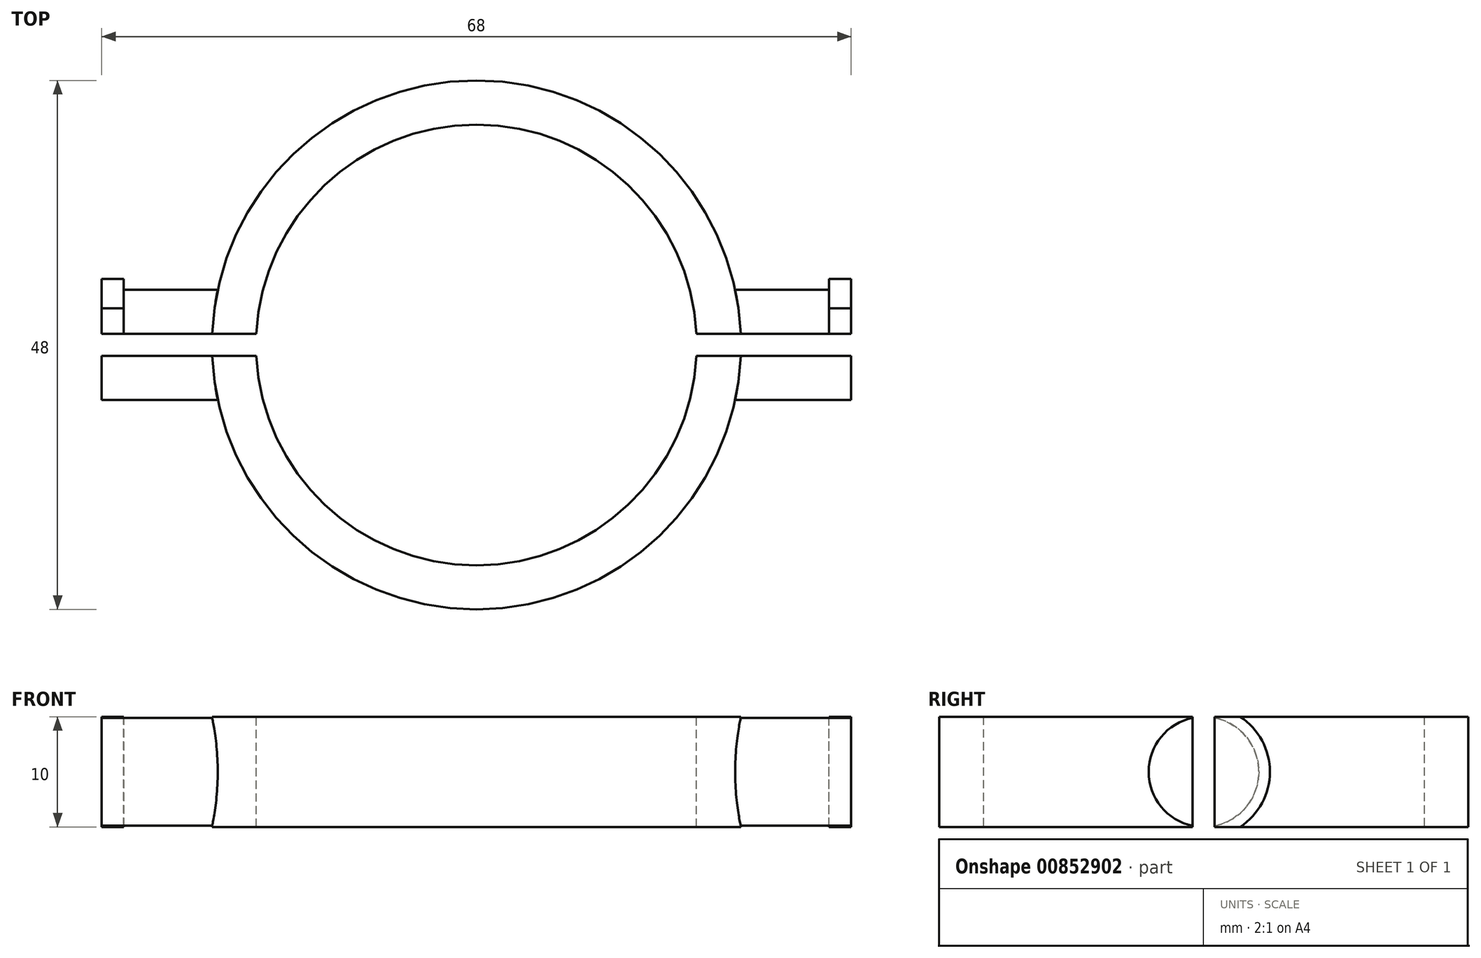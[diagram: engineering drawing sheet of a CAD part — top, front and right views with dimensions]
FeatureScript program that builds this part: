
annotation { "Feature Type Name" : "Feature", "Feature Type Description" : "" }
export const myFeature = defineFeature(function(context is Context, id is Id, definition is map)
    precondition{}
    {
        {
            assignVariable(context, id + "F0", {"name" : "MountDiameter", "anyValue" : 10});
        }
        {
            var Q0;
            Q0=qCreatedBy(makeId("Top.planeOp"),FACE);
            var sketch = newSketch(context, id + "F1", { "sketchPlane" : qUnion([Q0])});
            skCircle(sketch, "E0", {"center": v(0, 0) * mm, "radius": 20 * mm});
            skCircle(sketch, "E1", {"center": v(0, 0) * mm, "radius": 24 * mm});
            skLineSegment(sketch, "E2.bottom", {"start": v(23.47, 5) * mm, "end": v(34, 5) * mm});
            skLineSegment(sketch, "E2.top", {"start": v(23.47, -5) * mm, "end": v(34, -5) * mm});
            skLineSegment(sketch, "E2.left", {"start": v(23.47, 5) * mm, "end": v(23.47, -5) * mm});
            skLineSegment(sketch, "E2.right", {"start": v(34, 5) * mm, "end": v(34, -5) * mm});
            skLineSegment(sketch, "E3.bottom", {"start": v(-23.47, 5) * mm, "end": v(-34, 5) * mm});
            skLineSegment(sketch, "E3.top", {"start": v(-23.47, -5) * mm, "end": v(-34, -5) * mm});
            skLineSegment(sketch, "E3.left", {"start": v(-23.47, 5) * mm, "end": v(-23.47, -5) * mm});
            skLineSegment(sketch, "E3.right", {"start": v(-34, 5) * mm, "end": v(-34, -5) * mm});
            skSolve(sketch);
        }
        {
            var Q0;
            Q0=makeQuery(id+"F1.imprint","IMPRINT",FACE,{"disambiguationData":[TD([[makeQuery(id+"F1.imprint","IMPRINT",EDGE,{"derivedFrom":sQuery(id+"F1.wireOp",EDGE,"E0")}),-1.0]])]});
            var Q1;
            {var subQ1=sQuery(id+"F1.wireOp",EDGE,"E3.bottom");Q1=makeQuery(id+"F1.imprint","IMPRINT",FACE,{"disambiguationData":[TD([[makeQuery(id+"F1.imprint","IMPRINT",EDGE,{"derivedFrom":subQ1}),1.0]])]});}
            var Q2;
            {var subQ0=sQuery(id+"F1.wireOp",EDGE,"E3.left");Q2=makeQuery(id+"F1.imprint","IMPRINT",FACE,{"disambiguationData":[TD([[makeQuery(id+"F1.imprint","IMPRINT",EDGE,{"derivedFrom":subQ0}),-1.0]])]});}
            var Q3;
            {var subQ0=sQuery(id+"F1.wireOp",EDGE,"E2.left");Q3=makeQuery(id+"F1.imprint","IMPRINT",FACE,{"disambiguationData":[TD([[makeQuery(id+"F1.imprint","IMPRINT",EDGE,{"derivedFrom":subQ0}),1.0]])]});}
            var Q4;
            {var subQ1=sQuery(id+"F1.wireOp",EDGE,"E2.bottom");Q4=makeQuery(id+"F1.imprint","IMPRINT",FACE,{"disambiguationData":[TD([[makeQuery(id+"F1.imprint","IMPRINT",EDGE,{"derivedFrom":subQ1}),-1.0]])]});}
            extrude(context, id + "F2", {"entities" : qUnion([Q0, Q1, Q2, Q3, Q4]), "depth" : (getVariable(context, 'MountDiameter')) * mm, "offsetDistance" : 25 * mm});
        }
        {
            var Q0;
            Q0=makeQuery(id+"F2.opExtrude","CAP_EDGE",EDGE,{"disambiguationData":[OSD([sQuery(id+"F1.wireOp",EDGE,"E2.top")])],"isStart":false});
            var Q1;
            Q1=makeQuery(id+"F2.opExtrude","CAP_EDGE",EDGE,{"disambiguationData":[OSD([sQuery(id+"F1.wireOp",EDGE,"E2.bottom")])],"isStart":false});
            var Q2;
            Q2=makeQuery(id+"F2.opExtrude","CAP_EDGE",EDGE,{"disambiguationData":[OSD([sQuery(id+"F1.wireOp",EDGE,"E2.bottom")])],"isStart":true});
            var Q3;
            Q3=makeQuery(id+"F2.opExtrude","CAP_EDGE",EDGE,{"disambiguationData":[OSD([sQuery(id+"F1.wireOp",EDGE,"E2.top")])],"isStart":true});
            var Q4;
            Q4=makeQuery(id+"F2.opExtrude","CAP_EDGE",EDGE,{"disambiguationData":[OSD([sQuery(id+"F1.wireOp",EDGE,"E3.top")])],"isStart":false});
            var Q5;
            Q5=makeQuery(id+"F2.opExtrude","CAP_EDGE",EDGE,{"disambiguationData":[OSD([sQuery(id+"F1.wireOp",EDGE,"E3.top")])],"isStart":true});
            var Q6;
            Q6=makeQuery(id+"F2.opExtrude","CAP_EDGE",EDGE,{"disambiguationData":[OSD([sQuery(id+"F1.wireOp",EDGE,"E3.bottom")])],"isStart":true});
            var Q7;
            Q7=makeQuery(id+"F2.opExtrude","CAP_EDGE",EDGE,{"disambiguationData":[OSD([sQuery(id+"F1.wireOp",EDGE,"E3.bottom")])],"isStart":false});
            fillet(context, id + "F3", {"entities" : qUnion([Q0, Q1, Q2, Q3, Q4, Q5, Q6, Q7]), "radius" : (getVariable(context, 'MountDiameter') / 2) * mm, "tangentPropagation" : true, "allowEdgeOverflow" : false});
        }
        {
            var Q0;
            Q0=makeQuery(id+"F2.opExtrude","SWEPT_FACE",FACE,{"disambiguationData":[OSD([sQuery(id+"F1.wireOp",EDGE,"E2.right")])]});
            var sketch = newSketch(context, id + "F4", { "sketchPlane" : qUnion([Q0])});
            skCircle(sketch, "E4", {"center": v(0, 5) * mm, "radius": 6 * mm});
            skLineSegment(sketch, "E5", {"start": v(-3.32, 10) * mm, "end": v(3.32, 10) * mm});
            skLineSegment(sketch, "E6", {"start": v(-3.32, 0) * mm, "end": v(3.32, 0) * mm});
            skSolve(sketch);
        }
        {
            var Q0;
            {var subQ0=sQuery(id+"F4.wireOp",EDGE,"E5");var subQ1=sQuery(id+"F4.wireOp",EDGE,"E4");var subQ2=makeQuery(id+"F4.imprint","INTERSECT",VERTEX,{"disambiguationData":[OD(1.0)],"derivedFrom":[subQ1,subQ0]});Q0=makeQuery(id+"F4.imprint","IMPRINT",FACE,{"disambiguationData":[TD([[makeQuery(id+"F4.imprint","IMPRINT",EDGE,{"disambiguationData":[TD([[subQ2,1.0]])],"derivedFrom":subQ1}),1.0]])]});}
            extrude(context, id + "F5", {"entities" : qUnion([Q0]), "operationType" : NewBodyOperationType.ADD, "oppositeDirection" : true, "depth" : 2 * mm, "offsetDistance" : 25 * mm});
        }
        {
            var Q0;
            Q0=makeQuery(id+"F2.opExtrude","SWEPT_FACE",FACE,{"disambiguationData":[OSD([sQuery(id+"F1.wireOp",EDGE,"E3.right")])]});
            var sketch = newSketch(context, id + "F6", { "sketchPlane" : qUnion([Q0])});
            skCircle(sketch, "E7", {"center": v(0, 5) * mm, "radius": 6 * mm});
            skLineSegment(sketch, "E8", {"start": v(-3.32, 10) * mm, "end": v(3.32, 10) * mm});
            skLineSegment(sketch, "E9", {"start": v(-3.32, 0) * mm, "end": v(3.32, 0) * mm});
            skSolve(sketch);
        }
        {
            var Q0;
            {var subQ0=sQuery(id+"F6.wireOp",EDGE,"E8");var subQ1=sQuery(id+"F6.wireOp",EDGE,"E7");var subQ2=makeQuery(id+"F6.imprint","INTERSECT",VERTEX,{"disambiguationData":[OD(0.0)],"derivedFrom":[subQ1,subQ0]});Q0=makeQuery(id+"F6.imprint","IMPRINT",FACE,{"disambiguationData":[TD([[makeQuery(id+"F6.imprint","IMPRINT",EDGE,{"disambiguationData":[TD([[subQ2,-1.0]])],"derivedFrom":subQ1}),1.0]])]});}
            extrude(context, id + "F7", {"entities" : qUnion([Q0]), "operationType" : NewBodyOperationType.ADD, "oppositeDirection" : true, "depth" : 2 * mm, "offsetDistance" : 25 * mm});
        }
        {
            var Q0;
            Q0=makeQuery(id+"F2.opExtrude","CAP_FACE",FACE,{"disambiguationData":[OSD([sQuery(id+"F1.wireOp",EDGE,"E0"),sQuery(id+"F1.wireOp",EDGE,"E1"),sQuery(id+"F1.wireOp",EDGE,"E2.bottom"),sQuery(id+"F1.wireOp",EDGE,"E2.top"),sQuery(id+"F1.wireOp",EDGE,"E2.right"),sQuery(id+"F1.wireOp",EDGE,"E3.bottom"),sQuery(id+"F1.wireOp",EDGE,"E3.top"),sQuery(id+"F1.wireOp",EDGE,"E3.right")])],"isStart":false});
            var sketch = newSketch(context, id + "F8", { "sketchPlane" : qUnion([Q0])});
            skLineSegment(sketch, "E10.bottom", {"start": v(-35.84, 1) * mm, "end": v(39.88, 1) * mm});
            skLineSegment(sketch, "E10.top", {"start": v(-35.84, -1) * mm, "end": v(39.88, -1) * mm});
            skLineSegment(sketch, "E10.left", {"start": v(-35.84, 1) * mm, "end": v(-35.84, -1) * mm});
            skLineSegment(sketch, "E10.right", {"start": v(39.88, 1) * mm, "end": v(39.88, -1) * mm});
            skSolve(sketch);
        }
        {
            var Q0;
            {var subQ8=sQuery(id+"F8.wireOp",EDGE,"E10.right");Q0=makeQuery(id+"F8.imprint","IMPRINT",FACE,{"disambiguationData":[TD([[makeQuery(id+"F8.imprint","IMPRINT",EDGE,{"derivedFrom":subQ8}),-1.0]])]});}
            var Q1;
            {var subQ8=sQuery(id+"F8.wireOp",EDGE,"E10.bottom");var subQ10=makeQuery(id+"F2.opExtrude","CAP_EDGE",EDGE,{"disambiguationData":[OSD([sQuery(id+"F1.wireOp",EDGE,"E0")])],"isStart":false});var subQ12=makeQuery(id+"F8.imprint","INTERSECT",VERTEX,{"disambiguationData":[OD(1.0)],"derivedFrom":[subQ10,subQ8]});Q1=makeQuery(id+"F8.imprint","IMPRINT",FACE,{"disambiguationData":[TD([[makeQuery(id+"F8.imprint","IMPRINT",EDGE,{"disambiguationData":[TD([[subQ12,1.0]])],"derivedFrom":subQ10}),-1.0]])]});}
            var Q2;
            {var subQ8=sQuery(id+"F8.wireOp",EDGE,"E10.left");Q2=makeQuery(id+"F8.imprint","IMPRINT",FACE,{"disambiguationData":[TD([[makeQuery(id+"F8.imprint","IMPRINT",EDGE,{"derivedFrom":subQ8}),1.0]])]});}
            var Q3;
            {var subQ6=sQuery(id+"F8.wireOp",EDGE,"E10.bottom");var subQ10=makeQuery(id+"F2.opExtrude","CAP_EDGE",EDGE,{"disambiguationData":[OSD([sQuery(id+"F1.wireOp",EDGE,"E0")])],"isStart":false});var subQ12=makeQuery(id+"F8.imprint","INTERSECT",VERTEX,{"disambiguationData":[OD(0.0)],"derivedFrom":[subQ10,subQ6]});Q3=makeQuery(id+"F8.imprint","IMPRINT",FACE,{"disambiguationData":[TD([[makeQuery(id+"F8.imprint","IMPRINT",EDGE,{"disambiguationData":[TD([[subQ12,-1.0]])],"derivedFrom":subQ10}),-1.0]])]});}
            extrude(context, id + "F9", {"entities" : qUnion([Q0, Q1, Q2, Q3]), "operationType" : NewBodyOperationType.REMOVE, "oppositeDirection" : true, "depth" : 25 * mm, "offsetDistance" : 25 * mm});
        }
    });
